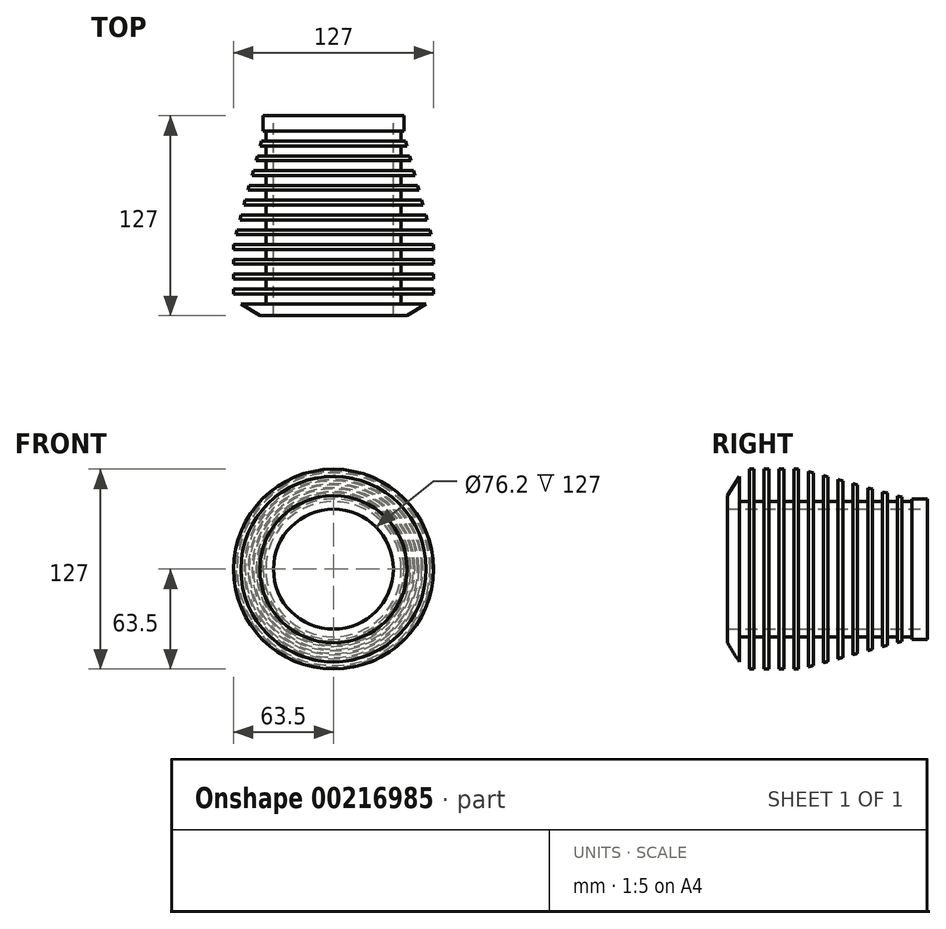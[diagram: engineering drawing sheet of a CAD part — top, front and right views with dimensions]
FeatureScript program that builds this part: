
annotation { "Feature Type Name" : "Feature", "Feature Type Description" : "" }
export const myFeature = defineFeature(function(context is Context, id is Id, definition is map)
    precondition{}
    {
        {
            var Q0;
            Q0=qCreatedBy(makeId("Front.planeOp"),FACE);
            var sketch = newSketch(context, id + "F0", { "sketchPlane" : qUnion([Q0])});
            skCircle(sketch, "E0", {"center": v(0, 0) * mm, "radius": 38.1 * mm});
            skCircle(sketch, "E1", {"center": v(0, 0) * mm, "radius": 63.5 * mm});
            skSolve(sketch);
        }
        {
            var Q0;
            Q0=makeQuery(id+"F0.imprint","IMPRINT",FACE,{"disambiguationData":[TD([[makeQuery(id+"F0.imprint","IMPRINT",EDGE,{"derivedFrom":sQuery(id+"F0.wireOp",EDGE,"E0")}),-1.0]])]});
            extrude(context, id + "F1", {"entities" : qUnion([Q0]), "depth" : 127 * mm});
        }
        {
            var Q0;
            Q0=qCreatedBy(makeId("Right.planeOp"),FACE);
            var sketch = newSketch(context, id + "F2", { "sketchPlane" : qUnion([Q0])});
            skLineSegment(sketch, "E2.bottom", {"start": v(-9.73, 42.96) * mm, "end": v(-16.08, 42.96) * mm});
            skLineSegment(sketch, "E2.top", {"start": v(-9.73, 83.6) * mm, "end": v(-16.08, 83.6) * mm});
            skLineSegment(sketch, "E2.left", {"start": v(-9.73, 42.96) * mm, "end": v(-9.73, 83.6) * mm});
            skLineSegment(sketch, "E2.right", {"start": v(-16.08, 42.96) * mm, "end": v(-16.08, 83.6) * mm});
            skPoint(sketch, "E2.middle", {"position": v(-12.9, 63.28) * mm});
            skLineSegment(sketch, "E3.1.0.0", {"start": v(-19.13, 42.96) * mm, "end": v(-19.13, 83.6) * mm});
            skLineSegment(sketch, "E3.1.0.1", {"start": v(-19.13, 83.6) * mm, "end": v(-25.48, 83.6) * mm});
            skLineSegment(sketch, "E3.1.0.2", {"start": v(-25.48, 42.96) * mm, "end": v(-25.48, 83.6) * mm});
            skLineSegment(sketch, "E3.1.0.3", {"start": v(-19.13, 42.96) * mm, "end": v(-25.48, 42.96) * mm});
            skLineSegment(sketch, "E3.2.0.0", {"start": v(-28.53, 42.96) * mm, "end": v(-28.53, 83.6) * mm});
            skLineSegment(sketch, "E3.2.0.1", {"start": v(-28.53, 83.6) * mm, "end": v(-34.88, 83.6) * mm});
            skLineSegment(sketch, "E3.2.0.2", {"start": v(-34.88, 42.96) * mm, "end": v(-34.88, 83.6) * mm});
            skLineSegment(sketch, "E3.2.0.3", {"start": v(-28.53, 42.96) * mm, "end": v(-34.88, 42.96) * mm});
            skLineSegment(sketch, "E3.3.0.0", {"start": v(-37.93, 42.96) * mm, "end": v(-37.93, 83.6) * mm});
            skLineSegment(sketch, "E3.3.0.1", {"start": v(-37.93, 83.6) * mm, "end": v(-44.28, 83.6) * mm});
            skLineSegment(sketch, "E3.3.0.2", {"start": v(-44.28, 42.96) * mm, "end": v(-44.28, 83.6) * mm});
            skLineSegment(sketch, "E3.3.0.3", {"start": v(-37.93, 42.96) * mm, "end": v(-44.28, 42.96) * mm});
            skLineSegment(sketch, "E3.4.0.0", {"start": v(-47.32, 42.96) * mm, "end": v(-47.32, 83.6) * mm});
            skLineSegment(sketch, "E3.4.0.1", {"start": v(-47.32, 83.6) * mm, "end": v(-53.67, 83.6) * mm});
            skLineSegment(sketch, "E3.4.0.2", {"start": v(-53.67, 42.96) * mm, "end": v(-53.67, 83.6) * mm});
            skLineSegment(sketch, "E3.4.0.3", {"start": v(-47.32, 42.96) * mm, "end": v(-53.67, 42.96) * mm});
            skLineSegment(sketch, "E3.5.0.0", {"start": v(-56.72, 42.96) * mm, "end": v(-56.72, 83.6) * mm});
            skLineSegment(sketch, "E3.5.0.1", {"start": v(-56.72, 83.6) * mm, "end": v(-63.07, 83.6) * mm});
            skLineSegment(sketch, "E3.5.0.2", {"start": v(-63.07, 42.96) * mm, "end": v(-63.07, 83.6) * mm});
            skLineSegment(sketch, "E3.5.0.3", {"start": v(-56.72, 42.96) * mm, "end": v(-63.07, 42.96) * mm});
            skLineSegment(sketch, "E3.6.0.0", {"start": v(-66.12, 42.96) * mm, "end": v(-66.12, 83.6) * mm});
            skLineSegment(sketch, "E3.6.0.1", {"start": v(-66.12, 83.6) * mm, "end": v(-72.47, 83.6) * mm});
            skLineSegment(sketch, "E3.6.0.2", {"start": v(-72.47, 42.96) * mm, "end": v(-72.47, 83.6) * mm});
            skLineSegment(sketch, "E3.6.0.3", {"start": v(-66.12, 42.96) * mm, "end": v(-72.47, 42.96) * mm});
            skLineSegment(sketch, "E3.7.0.0", {"start": v(-75.52, 42.96) * mm, "end": v(-75.52, 83.6) * mm});
            skLineSegment(sketch, "E3.7.0.1", {"start": v(-75.52, 83.6) * mm, "end": v(-81.87, 83.6) * mm});
            skLineSegment(sketch, "E3.7.0.2", {"start": v(-81.87, 42.96) * mm, "end": v(-81.87, 83.6) * mm});
            skLineSegment(sketch, "E3.7.0.3", {"start": v(-75.52, 42.96) * mm, "end": v(-81.87, 42.96) * mm});
            skLineSegment(sketch, "E3.8.0.0", {"start": v(-84.92, 42.96) * mm, "end": v(-84.92, 83.6) * mm});
            skLineSegment(sketch, "E3.8.0.1", {"start": v(-84.92, 83.6) * mm, "end": v(-91.27, 83.6) * mm});
            skLineSegment(sketch, "E3.8.0.2", {"start": v(-91.27, 42.96) * mm, "end": v(-91.27, 83.6) * mm});
            skLineSegment(sketch, "E3.8.0.3", {"start": v(-84.92, 42.96) * mm, "end": v(-91.27, 42.96) * mm});
            skLineSegment(sketch, "E3.9.0.0", {"start": v(-94.31, 42.96) * mm, "end": v(-94.31, 83.6) * mm});
            skLineSegment(sketch, "E3.9.0.1", {"start": v(-94.31, 83.6) * mm, "end": v(-100.66, 83.6) * mm});
            skLineSegment(sketch, "E3.9.0.2", {"start": v(-100.66, 42.96) * mm, "end": v(-100.66, 83.6) * mm});
            skLineSegment(sketch, "E3.9.0.3", {"start": v(-94.31, 42.96) * mm, "end": v(-100.66, 42.96) * mm});
            skLineSegment(sketch, "E3.10.0.0", {"start": v(-103.71, 42.96) * mm, "end": v(-103.71, 83.6) * mm});
            skLineSegment(sketch, "E3.10.0.1", {"start": v(-103.71, 83.6) * mm, "end": v(-110.06, 83.6) * mm});
            skLineSegment(sketch, "E3.10.0.2", {"start": v(-110.06, 42.96) * mm, "end": v(-110.06, 83.6) * mm});
            skLineSegment(sketch, "E3.10.0.3", {"start": v(-103.71, 42.96) * mm, "end": v(-110.06, 42.96) * mm});
            skLineSegment(sketch, "E3.11.0.0", {"start": v(-113.11, 42.96) * mm, "end": v(-113.11, 83.6) * mm});
            skLineSegment(sketch, "E3.11.0.1", {"start": v(-113.11, 83.6) * mm, "end": v(-119.46, 83.6) * mm});
            skLineSegment(sketch, "E3.11.0.2", {"start": v(-119.46, 42.96) * mm, "end": v(-119.46, 83.6) * mm});
            skLineSegment(sketch, "E3.11.0.3", {"start": v(-113.11, 42.96) * mm, "end": v(-119.46, 42.96) * mm});
            skLineSegment(sketch, "E3.direction1", {"start": v(-16.08, 42.96) * mm, "end": v(-25.48, 42.96) * mm, "construction": true});
            skSolve(sketch);
        }
        {
            var Q0;
            Q0=makeQuery(id+"F2.imprint","IMPRINT",FACE,{"disambiguationData":[TD([[makeQuery(id+"F2.imprint","IMPRINT",EDGE,{"derivedFrom":sQuery(id+"F2.wireOp",EDGE,"E2.bottom")}),-1.0]])]});
            var Q1;
            Q1=makeQuery(id+"F2.imprint","IMPRINT",FACE,{"disambiguationData":[TD([[makeQuery(id+"F2.imprint","IMPRINT",EDGE,{"derivedFrom":sQuery(id+"F2.wireOp",EDGE,"E3.1.0.0")}),1.0]])]});
            var Q2;
            Q2=makeQuery(id+"F2.imprint","IMPRINT",FACE,{"disambiguationData":[TD([[makeQuery(id+"F2.imprint","IMPRINT",EDGE,{"derivedFrom":sQuery(id+"F2.wireOp",EDGE,"E3.2.0.0")}),1.0]])]});
            var Q3;
            Q3=makeQuery(id+"F2.imprint","IMPRINT",FACE,{"disambiguationData":[TD([[makeQuery(id+"F2.imprint","IMPRINT",EDGE,{"derivedFrom":sQuery(id+"F2.wireOp",EDGE,"E3.3.0.0")}),1.0]])]});
            var Q4;
            Q4=makeQuery(id+"F2.imprint","IMPRINT",FACE,{"disambiguationData":[TD([[makeQuery(id+"F2.imprint","IMPRINT",EDGE,{"derivedFrom":sQuery(id+"F2.wireOp",EDGE,"E3.4.0.0")}),1.0]])]});
            var Q5;
            Q5=makeQuery(id+"F2.imprint","IMPRINT",FACE,{"disambiguationData":[TD([[makeQuery(id+"F2.imprint","IMPRINT",EDGE,{"derivedFrom":sQuery(id+"F2.wireOp",EDGE,"E3.5.0.0")}),1.0]])]});
            var Q6;
            Q6=makeQuery(id+"F2.imprint","IMPRINT",FACE,{"disambiguationData":[TD([[makeQuery(id+"F2.imprint","IMPRINT",EDGE,{"derivedFrom":sQuery(id+"F2.wireOp",EDGE,"E3.6.0.0")}),1.0]])]});
            var Q7;
            Q7=makeQuery(id+"F2.imprint","IMPRINT",FACE,{"disambiguationData":[TD([[makeQuery(id+"F2.imprint","IMPRINT",EDGE,{"derivedFrom":sQuery(id+"F2.wireOp",EDGE,"E3.7.0.0")}),1.0]])]});
            var Q8;
            Q8=makeQuery(id+"F2.imprint","IMPRINT",FACE,{"disambiguationData":[TD([[makeQuery(id+"F2.imprint","IMPRINT",EDGE,{"derivedFrom":sQuery(id+"F2.wireOp",EDGE,"E3.8.0.0")}),1.0]])]});
            var Q9;
            Q9=makeQuery(id+"F2.imprint","IMPRINT",FACE,{"disambiguationData":[TD([[makeQuery(id+"F2.imprint","IMPRINT",EDGE,{"derivedFrom":sQuery(id+"F2.wireOp",EDGE,"E3.9.0.0")}),1.0]])]});
            var Q10;
            Q10=makeQuery(id+"F2.imprint","IMPRINT",FACE,{"disambiguationData":[TD([[makeQuery(id+"F2.imprint","IMPRINT",EDGE,{"derivedFrom":sQuery(id+"F2.wireOp",EDGE,"E3.10.0.0")}),1.0]])]});
            var Q11;
            Q11=makeQuery(id+"F2.imprint","IMPRINT",FACE,{"disambiguationData":[TD([[makeQuery(id+"F2.imprint","IMPRINT",EDGE,{"derivedFrom":sQuery(id+"F2.wireOp",EDGE,"E3.11.0.0")}),1.0]])]});
            var Q12;
            Q12=makeQuery(id+"F1.opExtrude","CAP_EDGE",EDGE,{"disambiguationData":[OSD([sQuery(id+"F0.wireOp",EDGE,"E1")])],"isStart":true});
            revolve(context, id + "F3", {"operationType" : NewBodyOperationType.REMOVE, "entities" : qUnion([Q0, Q1, Q2, Q3, Q4, Q5, Q6, Q7, Q8, Q9, Q10, Q11]), "axis" : qUnion([Q12]), "revolveType" : RevolveType.FULL, "oppositeDirection" : true});
        }
        {
            var Q0;
            Q0=qCreatedBy(makeId("Right.planeOp"),FACE);
            var sketch = newSketch(context, id + "F4", { "sketchPlane" : qUnion([Q0])});
            skLineSegment(sketch, "E4", {"start": v(-132.08, 38.65) * mm, "end": v(-114.97, 66.03) * mm});
            skLineSegment(sketch, "E5", {"start": v(-114.97, 66.03) * mm, "end": v(-90.15, 66.03) * mm});
            skLineSegment(sketch, "E6", {"start": v(-90.15, 66.03) * mm, "end": v(-12, 44.64) * mm});
            skLineSegment(sketch, "E7", {"start": v(-12, 44.64) * mm, "end": v(6.55, 44.64) * mm});
            skLineSegment(sketch, "E8", {"start": v(6.55, 44.64) * mm, "end": v(6.55, 68.6) * mm});
            skLineSegment(sketch, "E9", {"start": v(6.55, 68.6) * mm, "end": v(-137.78, 68.6) * mm});
            skLineSegment(sketch, "E10", {"start": v(-137.78, 68.6) * mm, "end": v(-132.08, 38.65) * mm});
            skSolve(sketch);
        }
        {
            var Q0;
            Q0 = qSketchRegion(id + "F4", true);
            var Q1;
            Q1=makeQuery(id+"F1.opExtrude","CAP_EDGE",EDGE,{"disambiguationData":[OSD([sQuery(id+"F0.wireOp",EDGE,"E1")])],"isStart":false});
            revolve(context, id + "F5", {"operationType" : NewBodyOperationType.REMOVE, "entities" : qUnion([Q0]), "axis" : qUnion([Q1]), "revolveType" : RevolveType.FULL, "oppositeDirection" : true});
        }
    });
